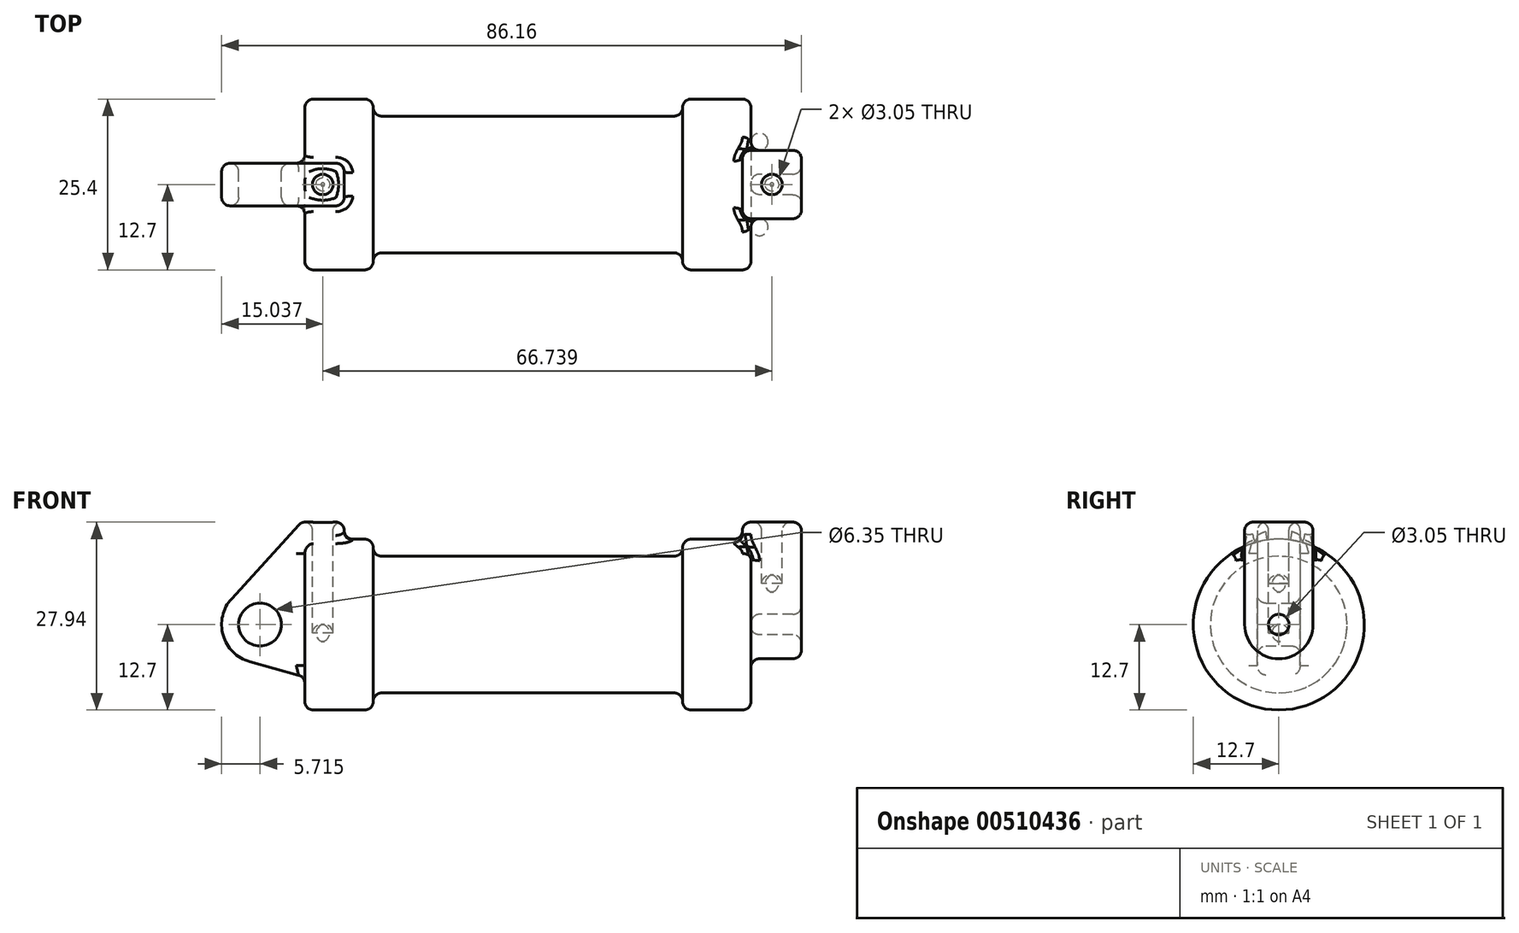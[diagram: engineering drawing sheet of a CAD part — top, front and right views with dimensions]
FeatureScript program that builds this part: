
annotation { "Feature Type Name" : "Feature", "Feature Type Description" : "" }
export const myFeature = defineFeature(function(context is Context, id is Id, definition is map)
    precondition{}
    {
        {
            var Q0;
            Q0=qCreatedBy(makeId("Front.planeOp"),FACE);
            var sketch = newSketch(context, id + "F0", { "sketchPlane" : qUnion([Q0])});
            skLineSegment(sketch, "E0", {"start": v(0, 0) * mm, "end": v(0, 12.7) * mm});
            skLineSegment(sketch, "E1", {"start": v(0, 12.7) * mm, "end": v(10.16, 12.7) * mm});
            skLineSegment(sketch, "E2", {"start": v(10.16, 12.7) * mm, "end": v(10.16, 10.16) * mm});
            skLineSegment(sketch, "E3", {"start": v(10.16, 10.16) * mm, "end": v(56.13, 10.16) * mm});
            skLineSegment(sketch, "E4", {"start": v(56.13, 10.16) * mm, "end": v(56.13, 12.7) * mm});
            skLineSegment(sketch, "E5", {"start": v(56.13, 12.7) * mm, "end": v(66.3, 12.7) * mm});
            skLineSegment(sketch, "E6", {"start": v(66.3, 12.7) * mm, "end": v(66.3, 0) * mm});
            skLineSegment(sketch, "E7", {"start": v(66.3, 0) * mm, "end": v(0, 0) * mm});
            skLineSegment(sketch, "E8", {"start": v(5.84, 15.24) * mm, "end": v(-0.5, 15.24) * mm});
            skLineSegment(sketch, "E9", {"start": v(-0.5, 15.24) * mm, "end": v(-10.88, 3.85) * mm});
            skLineSegment(sketch, "E10", {"start": v(0, 0) * mm, "end": v(-6.65, 0) * mm});
            skCircle(sketch, "E11", {"center": v(-6.65, 0) * mm, "radius": 5.72 * mm});
            skCircle(sketch, "E12", {"center": v(-6.65, 0) * mm, "radius": 3.18 * mm});
            skLineSegment(sketch, "E13", {"start": v(5.84, 15.24) * mm, "end": v(5.84, -9.4) * mm});
            skLineSegment(sketch, "E14", {"start": v(5.84, -9.4) * mm, "end": v(-8.18, -5.5) * mm});
            skSolve(sketch);
        }
        {
            var Q0;
            {var subQ0=sQuery(id+"F0.wireOp",EDGE,"E2");Q0=makeQuery(id+"F0.imprint","IMPRINT",FACE,{"disambiguationData":[TD([[makeQuery(id+"F0.imprint","IMPRINT",EDGE,{"derivedFrom":subQ0}),-1.0]])]});}
            var Q1;
            {var subQ0=sQuery(id+"F0.wireOp",EDGE,"E0");Q1=makeQuery(id+"F0.imprint","IMPRINT",FACE,{"disambiguationData":[TD([[makeQuery(id+"F0.imprint","IMPRINT",EDGE,{"derivedFrom":subQ0}),-1.0]])]});}
            var Q2;
            Q2=sQuery(id+"F0.wireOp",EDGE,"E7");
            revolve(context, id + "F1", {"entities" : qUnion([Q0, Q1]), "axis" : qUnion([Q2]), "revolveType" : RevolveType.FULL});
        }
        {
            var Q0;
            {var subQ5=sQuery(id+"F0.wireOp",EDGE,"E12");Q0=makeQuery(id+"F0.imprint","IMPRINT",FACE,{"disambiguationData":[TD([[makeQuery(id+"F0.imprint","IMPRINT",EDGE,{"derivedFrom":subQ5}),-1.0]])]});}
            var Q1;
            {var subQ0=sQuery(id+"F0.wireOp",EDGE,"E14");Q1=makeQuery(id+"F0.imprint","IMPRINT",FACE,{"disambiguationData":[TD([[makeQuery(id+"F0.imprint","IMPRINT",EDGE,{"derivedFrom":subQ0}),-1.0]])]});}
            var Q2;
            {var subQ0=sQuery(id+"F0.wireOp",EDGE,"E0");Q2=makeQuery(id+"F0.imprint","IMPRINT",FACE,{"disambiguationData":[TD([[makeQuery(id+"F0.imprint","IMPRINT",EDGE,{"derivedFrom":subQ0}),-1.0]])]});}
            var Q3;
            {var subQ1=sQuery(id+"F0.wireOp",EDGE,"E0");Q3=makeQuery(id+"F0.imprint","IMPRINT",FACE,{"disambiguationData":[TD([[makeQuery(id+"F0.imprint","IMPRINT",EDGE,{"derivedFrom":subQ1}),1.0]])]});}
            extrude(context, id + "F2", {"entities" : qUnion([Q0, Q1, Q2, Q3]), "operationType" : NewBodyOperationType.ADD, "endBound" : BoundingType.SYMMETRIC, "depth" : 6.35 * mm});
        }
        {
            var Q0;
            Q0=makeQuery(id+"F1.opRevolve","SWEPT_FACE",FACE,{"disambiguationData":[OSD([sQuery(id+"F0.wireOp",EDGE,"E6")])]});
            var sketch = newSketch(context, id + "F3", { "sketchPlane" : qUnion([Q0])});
            skCircle(sketch, "E15", {"center": v(0, 0) * mm, "radius": 1.52 * mm});
            skCircle(sketch, "E16", {"center": v(0, 0) * mm, "radius": 5.08 * mm});
            skLineSegment(sketch, "E17", {"start": v(5.08, 0) * mm, "end": v(5.08, 15.24) * mm});
            skLineSegment(sketch, "E18", {"start": v(-5.08, 0) * mm, "end": v(-5.08, 15.24) * mm});
            skLineSegment(sketch, "E19", {"start": v(-5.08, 15.24) * mm, "end": v(5.08, 15.24) * mm});
            skSolve(sketch);
        }
        {
            var Q0;
            Q0 = qSketchRegion(id + "F3", true);
            extrude(context, id + "F4", {"entities" : qUnion([Q0]), "operationType" : NewBodyOperationType.ADD, "depth" : 7.5 * mm, "hasSecondDirection" : true, "secondDirectionOppositeDirection" : true, "secondDirectionDepth" : 1.27 * mm});
        }
        {
            var Q0;
            Q0=makeQuery(id+"F2.opExtrude","SWEPT_FACE",FACE,{"disambiguationData":[OSD([sQuery(id+"F0.wireOp",EDGE,"E8")])]});
            var sketch = newSketch(context, id + "F5", { "sketchPlane" : qUnion([Q0])});
            skCircle(sketch, "E20", {"center": v(2.67, 0) * mm, "radius": 1.52 * mm});
            skPoint(sketch, "E20.centerSnap0", {"position": v(2.67, 3.18) * mm});
            skPoint(sketch, "E20.centerSnap1", {"position": v(-0.5, 0) * mm});
            skSolve(sketch);
        }
        {
            var Q0;
            Q0 = qSketchRegion(id + "F5", true);
            extrude(context, id + "F6", {"entities" : qUnion([Q0]), "operationType" : NewBodyOperationType.REMOVE, "oppositeDirection" : true, "depth" : 17.78 * mm});
        }
        {
            var Q0;
            Q0=makeQuery(id+"F4.opExtrude","SWEPT_FACE",FACE,{"disambiguationData":[OSD([sQuery(id+"F3.wireOp",EDGE,"E19")])]});
            var sketch = newSketch(context, id + "F7", { "sketchPlane" : qUnion([Q0])});
            skCircle(sketch, "E21", {"center": v(69.4, 0) * mm, "radius": 1.52 * mm});
            skPoint(sketch, "E21.centerSnap0", {"position": v(69.4, 5.08) * mm});
            skPoint(sketch, "E21.centerSnap1", {"position": v(65.02, 0) * mm});
            skSolve(sketch);
        }
        {
            var Q0;
            Q0 = qSketchRegion(id + "F7", true);
            extrude(context, id + "F8", {"entities" : qUnion([Q0]), "operationType" : NewBodyOperationType.REMOVE, "oppositeDirection" : true, "depth" : 10.4 * mm});
        }
        {
            var Q0;
            Q0=makeQuery(id+"F1.opRevolve","SWEPT_EDGE",EDGE,{"disambiguationData":[OSD([sQuery(id+"F0.wireOp",EDGE,"E2"),sQuery(id+"F0.wireOp",EDGE,"E3")])]});
            var Q1;
            Q1=makeQuery(id+"F4.opExtrude","SWEPT_FACE",FACE,{"disambiguationData":[OSD([sQuery(id+"F3.wireOp",EDGE,"E17")])]});
            var Q2;
            Q2=makeQuery(id+"F4.opExtrude","CAP_FACE",FACE,{"disambiguationData":[OSD([sQuery(id+"F3.wireOp",EDGE,"E15"),sQuery(id+"F3.wireOp",EDGE,"E16"),sQuery(id+"F3.wireOp",EDGE,"E17"),sQuery(id+"F3.wireOp",EDGE,"E18"),sQuery(id+"F3.wireOp",EDGE,"E19")])],"isStart":true});
            var Q3;
            Q3=makeQuery(id+"F4.opExtrude","SWEPT_FACE",FACE,{"disambiguationData":[OSD([sQuery(id+"F3.wireOp",EDGE,"E15")])]});
            var Q4;
            Q4=makeQuery(id+"F4.boolean.opBoolean","SPLIT",FACE,{"disambiguationData":[TD([makeQuery(id+"F4.opExtrude","SWEPT_FACE",FACE,{"disambiguationData":[OSD([sQuery(id+"F3.wireOp",EDGE,"E15")])]})])],"derivedFrom":makeQuery(id+"F1.opRevolve","SWEPT_FACE",FACE,{"disambiguationData":[OSD([sQuery(id+"F0.wireOp",EDGE,"E6")])]})});
            var Q5;
            Q5=makeQuery(id+"F4.opExtrude","SWEPT_FACE",FACE,{"disambiguationData":[OSD([sQuery(id+"F3.wireOp",EDGE,"E18")])]});
            var Q6;
            Q6=makeQuery(id+"F4.opExtrude","SWEPT_FACE",FACE,{"disambiguationData":[OSD([sQuery(id+"F3.wireOp",EDGE,"E19")])]});
            var Q7;
            Q7=makeQuery(id+"F2.boolean.opBoolean","INTERSECT",EDGE,{"derivedFrom":[makeQuery(id+"F1.opRevolve","SWEPT_FACE",FACE,{"disambiguationData":[OSD([sQuery(id+"F0.wireOp",EDGE,"E0")])]}),makeQuery(id+"F2.opExtrude","SWEPT_FACE",FACE,{"disambiguationData":[OSD([sQuery(id+"F0.wireOp",EDGE,"E14")])]})]});
            var Q8;
            Q8=makeQuery(id+"F4.opExtrude","CAP_FACE",FACE,{"disambiguationData":[OSD([sQuery(id+"F3.wireOp",EDGE,"E15"),sQuery(id+"F3.wireOp",EDGE,"E16"),sQuery(id+"F3.wireOp",EDGE,"E17"),sQuery(id+"F3.wireOp",EDGE,"E18"),sQuery(id+"F3.wireOp",EDGE,"E19")])],"isStart":false});
            var Q9;
            Q9=makeQuery(id+"F4.boolean.opBoolean","INTERSECT",EDGE,{"derivedFrom":[makeQuery(id+"F1.opRevolve","SWEPT_FACE",FACE,{"disambiguationData":[OSD([sQuery(id+"F0.wireOp",EDGE,"E5")])]}),makeQuery(id+"F4.opExtrude","CAP_FACE",FACE,{"disambiguationData":[OSD([sQuery(id+"F3.wireOp",EDGE,"E15"),sQuery(id+"F3.wireOp",EDGE,"E16"),sQuery(id+"F3.wireOp",EDGE,"E17"),sQuery(id+"F3.wireOp",EDGE,"E18"),sQuery(id+"F3.wireOp",EDGE,"E19")])],"isStart":true})]});
            var Q10;
            Q10=makeQuery(id+"F8.boolean.opBoolean","COPY",FACE,{"derivedFrom":makeQuery(id+"F8.opExtrude","SWEPT_FACE",FACE,{"disambiguationData":[OSD([sQuery(id+"F7.wireOp",EDGE,"E21")])]})});
            var Q11;
            Q11=makeQuery(id+"F8.boolean.opBoolean","COPY",FACE,{"derivedFrom":makeQuery(id+"F8.opExtrude","CAP_FACE",FACE,{"disambiguationData":[OSD([sQuery(id+"F7.wireOp",EDGE,"E21")])],"isStart":false})});
            var Q12;
            Q12=makeQuery(id+"F2.opExtrude","CAP_EDGE",EDGE,{"disambiguationData":[OSD([sQuery(id+"F0.wireOp",EDGE,"E14")])],"isStart":true});
            var Q13;
            Q13=makeQuery(id+"F4.boolean.opBoolean","INTERSECT",EDGE,{"derivedFrom":[makeQuery(id+"F1.opRevolve","SWEPT_FACE",FACE,{"disambiguationData":[OSD([sQuery(id+"F0.wireOp",EDGE,"E6")])]}),makeQuery(id+"F4.opExtrude","SWEPT_FACE",FACE,{"disambiguationData":[OSD([sQuery(id+"F3.wireOp",EDGE,"E16")])]})]});
            var Q14;
            Q14=makeQuery(id+"F4.boolean.opBoolean","INTERSECT",EDGE,{"derivedFrom":[makeQuery(id+"F1.opRevolve","SWEPT_FACE",FACE,{"disambiguationData":[OSD([sQuery(id+"F0.wireOp",EDGE,"E5")])]}),makeQuery(id+"F4.opExtrude","SWEPT_FACE",FACE,{"disambiguationData":[OSD([sQuery(id+"F3.wireOp",EDGE,"E17")])]})]});
            var Q15;
            Q15=makeQuery(id+"F4.boolean.opBoolean","INTERSECT",EDGE,{"derivedFrom":[makeQuery(id+"F1.opRevolve","SWEPT_FACE",FACE,{"disambiguationData":[OSD([sQuery(id+"F0.wireOp",EDGE,"E5")])]}),makeQuery(id+"F4.opExtrude","SWEPT_FACE",FACE,{"disambiguationData":[OSD([sQuery(id+"F3.wireOp",EDGE,"E18")])]})]});
            var Q16;
            Q16=makeQuery(id+"F4.opExtrude","CAP_EDGE",EDGE,{"disambiguationData":[OSD([sQuery(id+"F3.wireOp",EDGE,"E17")])],"isStart":false});
            var Q17;
            Q17=makeQuery(id+"F4.boolean.opBoolean","INTERSECT",EDGE,{"derivedFrom":[makeQuery(id+"F1.opRevolve","SWEPT_FACE",FACE,{"disambiguationData":[OSD([sQuery(id+"F0.wireOp",EDGE,"E6")])]}),makeQuery(id+"F4.opExtrude","SWEPT_FACE",FACE,{"disambiguationData":[OSD([sQuery(id+"F3.wireOp",EDGE,"E15")])]})]});
            var Q18;
            Q18=makeQuery(id+"F4.boolean.opBoolean","INTERSECT",EDGE,{"derivedFrom":[makeQuery(id+"F1.opRevolve","SWEPT_FACE",FACE,{"disambiguationData":[OSD([sQuery(id+"F0.wireOp",EDGE,"E6")])]}),makeQuery(id+"F4.opExtrude","SWEPT_FACE",FACE,{"disambiguationData":[OSD([sQuery(id+"F3.wireOp",EDGE,"E17")])]})]});
            var Q19;
            Q19=makeQuery(id+"F4.boolean.opBoolean","INTERSECT",EDGE,{"derivedFrom":[makeQuery(id+"F1.opRevolve","SWEPT_FACE",FACE,{"disambiguationData":[OSD([sQuery(id+"F0.wireOp",EDGE,"E6")])]}),makeQuery(id+"F4.opExtrude","SWEPT_FACE",FACE,{"disambiguationData":[OSD([sQuery(id+"F3.wireOp",EDGE,"E18")])]})]});
            var Q20;
            Q20=makeQuery(id+"F4.opExtrude","SWEPT_EDGE",EDGE,{"disambiguationData":[OSD([sQuery(id+"F3.wireOp",EDGE,"E16"),sQuery(id+"F3.wireOp",EDGE,"E17")])]});
            var Q21;
            Q21=makeQuery(id+"F4.opExtrude","SWEPT_EDGE",EDGE,{"disambiguationData":[OSD([sQuery(id+"F3.wireOp",EDGE,"E17"),sQuery(id+"F3.wireOp",EDGE,"E19")])]});
            var Q22;
            Q22=makeQuery(id+"F4.opExtrude","SWEPT_EDGE",EDGE,{"disambiguationData":[OSD([sQuery(id+"F3.wireOp",EDGE,"E18"),sQuery(id+"F3.wireOp",EDGE,"E19")])]});
            var Q23;
            Q23=makeQuery(id+"F4.opExtrude","CAP_EDGE",EDGE,{"disambiguationData":[OSD([sQuery(id+"F3.wireOp",EDGE,"E18")])],"isStart":false});
            var Q24;
            Q24=makeQuery(id+"F4.opExtrude","CAP_EDGE",EDGE,{"disambiguationData":[OSD([sQuery(id+"F3.wireOp",EDGE,"E19")])],"isStart":false});
            var Q25;
            Q25=makeQuery(id+"F6.boolean.opBoolean","COPY",FACE,{"derivedFrom":makeQuery(id+"F6.opExtrude","CAP_FACE",FACE,{"disambiguationData":[OSD([sQuery(id+"F5.wireOp",EDGE,"E20")])],"isStart":false})});
            var Q26;
            Q26=makeQuery(id+"F4.opExtrude","CAP_EDGE",EDGE,{"disambiguationData":[OSD([sQuery(id+"F3.wireOp",EDGE,"E16")])],"isStart":false});
            var Q27;
            Q27=makeQuery(id+"F4.opExtrude","CAP_EDGE",EDGE,{"disambiguationData":[OSD([sQuery(id+"F3.wireOp",EDGE,"E19")])],"isStart":true});
            var Q28;
            Q28=makeQuery(id+"F6.boolean.opBoolean","COPY",EDGE,{"derivedFrom":makeQuery(id+"F6.opExtrude","CAP_EDGE",EDGE,{"disambiguationData":[OSD([sQuery(id+"F5.wireOp",EDGE,"E20")])],"isStart":false})});
            var Q29;
            Q29=makeQuery(id+"F8.boolean.opBoolean","COPY",EDGE,{"derivedFrom":makeQuery(id+"F8.opExtrude","CAP_EDGE",EDGE,{"disambiguationData":[OSD([sQuery(id+"F7.wireOp",EDGE,"E21")])],"isStart":false})});
            var Q30;
            Q30=makeQuery(id+"F8.boolean.opBoolean","COPY",EDGE,{"derivedFrom":makeQuery(id+"F8.opExtrude","CAP_EDGE",EDGE,{"disambiguationData":[OSD([sQuery(id+"F7.wireOp",EDGE,"E21")])],"isStart":true})});
            var Q31;
            Q31=makeQuery(id+"F2.opExtrude","CAP_EDGE",EDGE,{"disambiguationData":[OSD([sQuery(id+"F0.wireOp",EDGE,"E11")])],"isStart":true});
            var Q32;
            Q32=makeQuery(id+"F2.opExtrude","CAP_EDGE",EDGE,{"disambiguationData":[OSD([sQuery(id+"F0.wireOp",EDGE,"E12")])],"isStart":true});
            var Q33;
            Q33=makeQuery(id+"F4.opExtrude","SWEPT_FACE",FACE,{"disambiguationData":[OSD([sQuery(id+"F3.wireOp",EDGE,"E16")])]});
            var Q34;
            Q34=makeQuery(id+"F4.opExtrude","SWEPT_EDGE",EDGE,{"disambiguationData":[OSD([sQuery(id+"F3.wireOp",EDGE,"E16"),sQuery(id+"F3.wireOp",EDGE,"E18")])]});
            var Q35;
            Q35=makeQuery(id+"F4.opExtrude","CAP_EDGE",EDGE,{"disambiguationData":[OSD([sQuery(id+"F3.wireOp",EDGE,"E18")])],"isStart":true});
            var Q36;
            Q36=makeQuery(id+"F4.opExtrude","CAP_EDGE",EDGE,{"disambiguationData":[OSD([sQuery(id+"F3.wireOp",EDGE,"E15")])],"isStart":false});
            var Q37;
            Q37=makeQuery(id+"F4.opExtrude","CAP_EDGE",EDGE,{"disambiguationData":[OSD([sQuery(id+"F3.wireOp",EDGE,"E17")])],"isStart":true});
            var Q38;
            Q38=makeQuery(id+"F2.opExtrude","SWEPT_FACE",FACE,{"disambiguationData":[OSD([sQuery(id+"F0.wireOp",EDGE,"E12")])]});
            var Q39;
            Q39=makeQuery(id+"F1.opRevolve","SWEPT_EDGE",EDGE,{"disambiguationData":[OSD([sQuery(id+"F0.wireOp",EDGE,"E3"),sQuery(id+"F0.wireOp",EDGE,"E4")])]});
            var Q40;
            Q40=makeQuery(id+"F2.opExtrude","CAP_EDGE",EDGE,{"disambiguationData":[OSD([sQuery(id+"F0.wireOp",EDGE,"E9")])],"isStart":true});
            var Q41;
            Q41=makeQuery(id+"F1.opRevolve","SWEPT_EDGE",EDGE,{"disambiguationData":[OSD([sQuery(id+"F0.wireOp",EDGE,"E0"),sQuery(id+"F0.wireOp",EDGE,"E1")])]});
            var Q42;
            Q42=makeQuery(id+"F2.opExtrude","SWEPT_FACE",FACE,{"disambiguationData":[OSD([sQuery(id+"F0.wireOp",EDGE,"E11")])]});
            var Q43;
            Q43=makeQuery(id+"F1.opRevolve","SWEPT_FACE",FACE,{"disambiguationData":[OSD([sQuery(id+"F0.wireOp",EDGE,"E4")])]});
            var Q44;
            Q44=makeQuery(id+"F2.opExtrude","SWEPT_FACE",FACE,{"disambiguationData":[OSD([sQuery(id+"F0.wireOp",EDGE,"E8")])]});
            var Q45;
            Q45=makeQuery(id+"F4.boolean.opBoolean","SPLIT",FACE,{"disambiguationData":[TD([makeQuery(id+"F1.opRevolve","SWEPT_FACE",FACE,{"disambiguationData":[OSD([sQuery(id+"F0.wireOp",EDGE,"E5")])]})])],"derivedFrom":makeQuery(id+"F1.opRevolve","SWEPT_FACE",FACE,{"disambiguationData":[OSD([sQuery(id+"F0.wireOp",EDGE,"E6")])]})});
            var Q46;
            Q46=makeQuery(id+"F1.opRevolve","SWEPT_EDGE",EDGE,{"disambiguationData":[OSD([sQuery(id+"F0.wireOp",EDGE,"E1"),sQuery(id+"F0.wireOp",EDGE,"E2")])]});
            var Q47;
            Q47=makeQuery(id+"F2.opExtrude","CAP_FACE",FACE,{"disambiguationData":[OSD([sQuery(id+"F0.wireOp",EDGE,"E8"),sQuery(id+"F0.wireOp",EDGE,"E9"),sQuery(id+"F0.wireOp",EDGE,"E11"),sQuery(id+"F0.wireOp",EDGE,"E12"),sQuery(id+"F0.wireOp",EDGE,"E13"),sQuery(id+"F0.wireOp",EDGE,"E14")])],"isStart":false});
            var Q48;
            Q48=makeQuery(id+"F2.opExtrude","CAP_EDGE",EDGE,{"disambiguationData":[OSD([sQuery(id+"F0.wireOp",EDGE,"E14")])],"isStart":false});
            var Q49;
            Q49=makeQuery(id+"F1.opRevolve","SWEPT_FACE",FACE,{"disambiguationData":[OSD([sQuery(id+"F0.wireOp",EDGE,"E5")])]});
            var Q50;
            Q50=makeQuery(id+"F2.opExtrude","SWEPT_FACE",FACE,{"disambiguationData":[OSD([sQuery(id+"F0.wireOp",EDGE,"E9")])]});
            var Q51;
            Q51=makeQuery(id+"F2.opExtrude","CAP_EDGE",EDGE,{"disambiguationData":[OSD([sQuery(id+"F0.wireOp",EDGE,"E11")])],"isStart":false});
            var Q52;
            Q52=makeQuery(id+"F1.opRevolve","SWEPT_FACE",FACE,{"disambiguationData":[OSD([sQuery(id+"F0.wireOp",EDGE,"E3")])]});
            var Q53;
            Q53=makeQuery(id+"F1.opRevolve","SWEPT_FACE",FACE,{"disambiguationData":[OSD([sQuery(id+"F0.wireOp",EDGE,"E1")])]});
            var Q54;
            Q54=makeQuery(id+"F1.opRevolve","SWEPT_FACE",FACE,{"disambiguationData":[OSD([sQuery(id+"F0.wireOp",EDGE,"E0")])]});
            var Q55;
            Q55=makeQuery(id+"F2.opExtrude","CAP_EDGE",EDGE,{"disambiguationData":[OSD([sQuery(id+"F0.wireOp",EDGE,"E8")])],"isStart":false});
            var Q56;
            Q56=makeQuery(id+"F2.opExtrude","CAP_FACE",FACE,{"disambiguationData":[OSD([sQuery(id+"F0.wireOp",EDGE,"E8"),sQuery(id+"F0.wireOp",EDGE,"E9"),sQuery(id+"F0.wireOp",EDGE,"E11"),sQuery(id+"F0.wireOp",EDGE,"E12"),sQuery(id+"F0.wireOp",EDGE,"E13"),sQuery(id+"F0.wireOp",EDGE,"E14")])],"isStart":true});
            var Q57;
            Q57=makeQuery(id+"F1.opRevolve","SWEPT_EDGE",EDGE,{"disambiguationData":[OSD([sQuery(id+"F0.wireOp",EDGE,"E4"),sQuery(id+"F0.wireOp",EDGE,"E5")])]});
            var Q58;
            Q58=makeQuery(id+"F2.opExtrude","CAP_EDGE",EDGE,{"disambiguationData":[OSD([sQuery(id+"F0.wireOp",EDGE,"E12")])],"isStart":false});
            var Q59;
            Q59=makeQuery(id+"F1.opRevolve","SWEPT_FACE",FACE,{"disambiguationData":[OSD([sQuery(id+"F0.wireOp",EDGE,"E2")])]});
            var Q60;
            Q60=makeQuery(id+"F1.opRevolve","SWEPT_EDGE",EDGE,{"disambiguationData":[OSD([sQuery(id+"F0.wireOp",EDGE,"E5"),sQuery(id+"F0.wireOp",EDGE,"E6")])]});
            var Q61;
            Q61=makeQuery(id+"F2.opExtrude","CAP_EDGE",EDGE,{"disambiguationData":[OSD([sQuery(id+"F0.wireOp",EDGE,"E9")])],"isStart":false});
            var Q62;
            Q62=makeQuery(id+"F2.opExtrude","SWEPT_EDGE",EDGE,{"disambiguationData":[OSD([sQuery(id+"F0.wireOp",EDGE,"E8"),sQuery(id+"F0.wireOp",EDGE,"E9")])]});
            var Q63;
            Q63=makeQuery(id+"F2.opExtrude","SWEPT_FACE",FACE,{"disambiguationData":[OSD([sQuery(id+"F0.wireOp",EDGE,"E14")])]});
            var Q64;
            Q64=makeQuery(id+"F2.opExtrude","SWEPT_EDGE",EDGE,{"disambiguationData":[OSD([sQuery(id+"F0.wireOp",EDGE,"E8"),sQuery(id+"F0.wireOp",EDGE,"E13")])]});
            var Q65;
            Q65=makeQuery(id+"F2.opExtrude","SWEPT_EDGE",EDGE,{"disambiguationData":[OSD([sQuery(id+"F0.wireOp",EDGE,"E11"),sQuery(id+"F0.wireOp",EDGE,"E14")])]});
            var Q66;
            Q66=makeQuery(id+"F2.opExtrude","CAP_EDGE",EDGE,{"disambiguationData":[OSD([sQuery(id+"F0.wireOp",EDGE,"E13")])],"isStart":false});
            var Q67;
            Q67=makeQuery(id+"F2.boolean.opBoolean","INTERSECT",EDGE,{"derivedFrom":[makeQuery(id+"F1.opRevolve","SWEPT_FACE",FACE,{"disambiguationData":[OSD([sQuery(id+"F0.wireOp",EDGE,"E0")])]}),makeQuery(id+"F2.opExtrude","CAP_FACE",FACE,{"disambiguationData":[OSD([sQuery(id+"F0.wireOp",EDGE,"E8"),sQuery(id+"F0.wireOp",EDGE,"E9"),sQuery(id+"F0.wireOp",EDGE,"E11"),sQuery(id+"F0.wireOp",EDGE,"E12"),sQuery(id+"F0.wireOp",EDGE,"E13"),sQuery(id+"F0.wireOp",EDGE,"E14")])],"isStart":false})]});
            var Q68;
            Q68=makeQuery(id+"F2.boolean.opBoolean","INTERSECT",EDGE,{"derivedFrom":[makeQuery(id+"F1.opRevolve","SWEPT_FACE",FACE,{"disambiguationData":[OSD([sQuery(id+"F0.wireOp",EDGE,"E0")])]}),makeQuery(id+"F2.opExtrude","CAP_FACE",FACE,{"disambiguationData":[OSD([sQuery(id+"F0.wireOp",EDGE,"E8"),sQuery(id+"F0.wireOp",EDGE,"E9"),sQuery(id+"F0.wireOp",EDGE,"E11"),sQuery(id+"F0.wireOp",EDGE,"E12"),sQuery(id+"F0.wireOp",EDGE,"E13"),sQuery(id+"F0.wireOp",EDGE,"E14")])],"isStart":true})]});
            var Q69;
            Q69=makeQuery(id+"F2.opExtrude","CAP_EDGE",EDGE,{"disambiguationData":[OSD([sQuery(id+"F0.wireOp",EDGE,"E8")])],"isStart":true});
            var Q70;
            Q70=makeQuery(id+"F6.boolean.opBoolean","COPY",FACE,{"derivedFrom":makeQuery(id+"F6.opExtrude","SWEPT_FACE",FACE,{"disambiguationData":[OSD([sQuery(id+"F5.wireOp",EDGE,"E20")])]})});
            var Q71;
            Q71=makeQuery(id+"F2.opExtrude","SWEPT_EDGE",EDGE,{"disambiguationData":[OSD([sQuery(id+"F0.wireOp",EDGE,"E9"),sQuery(id+"F0.wireOp",EDGE,"E11")])]});
            var Q72;
            Q72=makeQuery(id+"F6.boolean.opBoolean","COPY",EDGE,{"derivedFrom":makeQuery(id+"F6.opExtrude","CAP_EDGE",EDGE,{"disambiguationData":[OSD([sQuery(id+"F5.wireOp",EDGE,"E20")])],"isStart":true})});
            var Q73;
            Q73=makeQuery(id+"F2.boolean.opBoolean","INTERSECT",EDGE,{"derivedFrom":[makeQuery(id+"F1.opRevolve","SWEPT_FACE",FACE,{"disambiguationData":[OSD([sQuery(id+"F0.wireOp",EDGE,"E1")])]}),makeQuery(id+"F2.opExtrude","CAP_FACE",FACE,{"disambiguationData":[OSD([sQuery(id+"F0.wireOp",EDGE,"E8"),sQuery(id+"F0.wireOp",EDGE,"E9"),sQuery(id+"F0.wireOp",EDGE,"E11"),sQuery(id+"F0.wireOp",EDGE,"E12"),sQuery(id+"F0.wireOp",EDGE,"E13"),sQuery(id+"F0.wireOp",EDGE,"E14")])],"isStart":false})]});
            var Q74;
            Q74=makeQuery(id+"F2.boolean.opBoolean","INTERSECT",EDGE,{"derivedFrom":[makeQuery(id+"F1.opRevolve","SWEPT_FACE",FACE,{"disambiguationData":[OSD([sQuery(id+"F0.wireOp",EDGE,"E1")])]}),makeQuery(id+"F2.opExtrude","CAP_FACE",FACE,{"disambiguationData":[OSD([sQuery(id+"F0.wireOp",EDGE,"E8"),sQuery(id+"F0.wireOp",EDGE,"E9"),sQuery(id+"F0.wireOp",EDGE,"E11"),sQuery(id+"F0.wireOp",EDGE,"E12"),sQuery(id+"F0.wireOp",EDGE,"E13"),sQuery(id+"F0.wireOp",EDGE,"E14")])],"isStart":true})]});
            var Q75;
            Q75=makeQuery(id+"F2.opExtrude","SWEPT_FACE",FACE,{"disambiguationData":[OSD([sQuery(id+"F0.wireOp",EDGE,"E13")])]});
            var Q76;
            Q76=makeQuery(id+"F2.boolean.opBoolean","INTERSECT",EDGE,{"derivedFrom":[makeQuery(id+"F1.opRevolve","SWEPT_FACE",FACE,{"disambiguationData":[OSD([sQuery(id+"F0.wireOp",EDGE,"E1")])]}),makeQuery(id+"F2.opExtrude","SWEPT_FACE",FACE,{"disambiguationData":[OSD([sQuery(id+"F0.wireOp",EDGE,"E13")])]})]});
            var Q77;
            Q77=makeQuery(id+"F2.opExtrude","CAP_EDGE",EDGE,{"disambiguationData":[OSD([sQuery(id+"F0.wireOp",EDGE,"E13")])],"isStart":true});
            fillet(context, id + "F9", {"entities" : qUnion([Q0, Q1, Q2, Q3, Q4, Q5, Q6, Q7, Q8, Q9, Q10, Q11, Q12, Q13, Q14, Q15, Q16, Q17, Q18, Q19, Q20, Q21, Q22, Q23, Q24, Q25, Q26, Q27, Q28, Q29, Q30, Q31, Q32, Q33, Q34, Q35, Q36, Q37, Q38, Q39, Q40, Q41, Q42, Q43, Q44, Q45, Q46, Q47, Q48, Q49, Q50, Q51, Q52, Q53, Q54, Q55, Q56, Q57, Q58, Q59, Q60, Q61, Q62, Q63, Q64, Q65, Q66, Q67, Q68, Q69, Q70, Q71, Q72, Q73, Q74, Q75, Q76, Q77]), "radius" : 1.27 * mm, "tangentPropagation" : true, "allowEdgeOverflow" : false});
        }
    });
